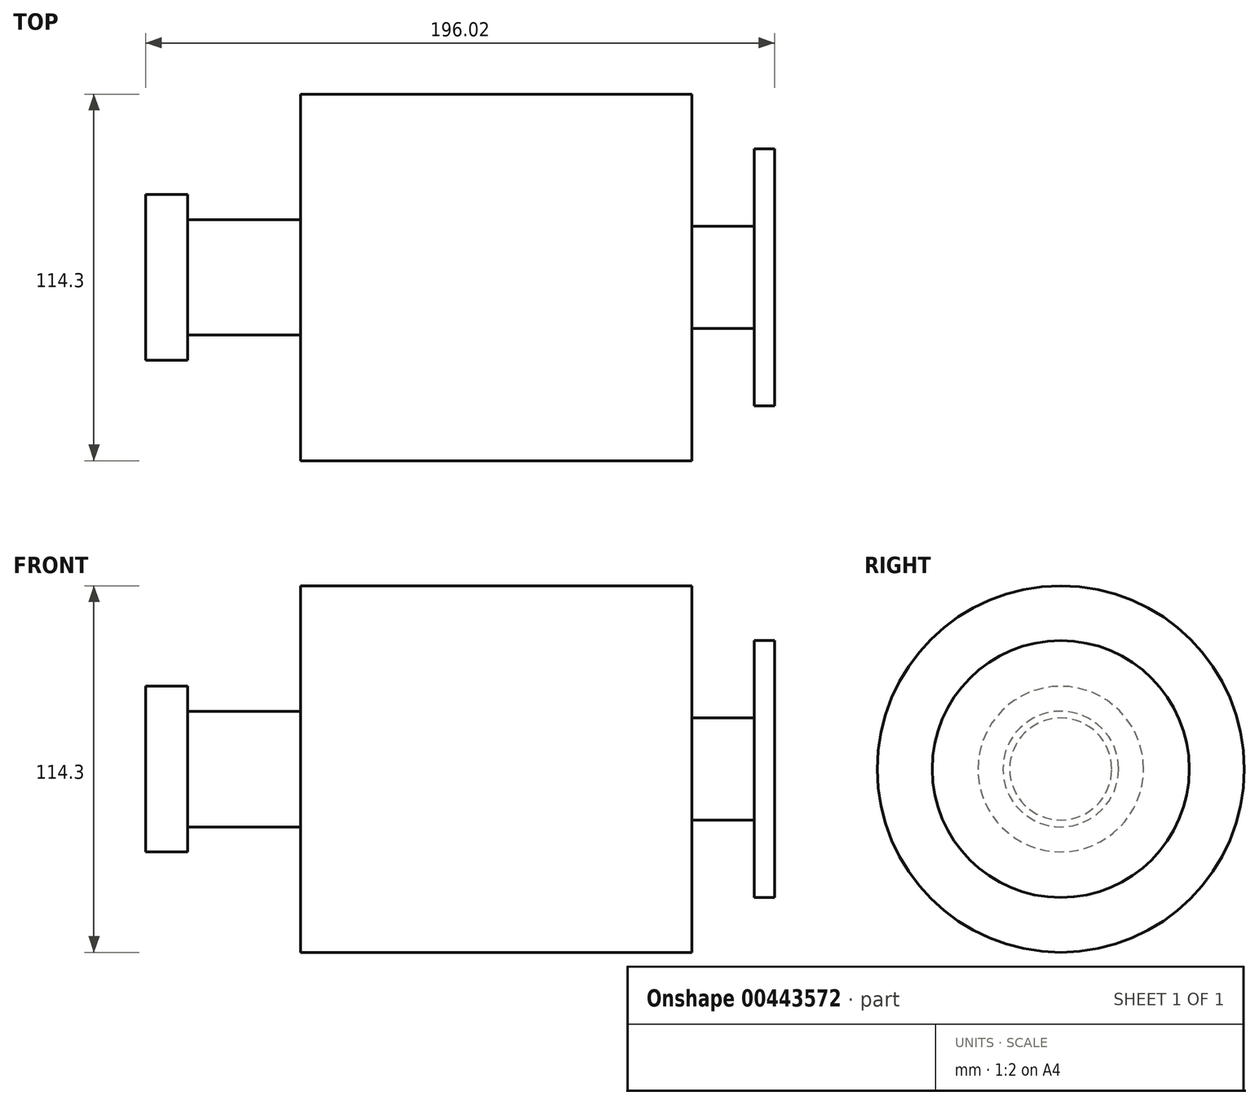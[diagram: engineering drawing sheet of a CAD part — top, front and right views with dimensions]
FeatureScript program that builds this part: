
annotation { "Feature Type Name" : "Feature", "Feature Type Description" : "" }
export const myFeature = defineFeature(function(context is Context, id is Id, definition is map)
    precondition{}
    {
        {
            var Q0;
            Q0=qCreatedBy(makeId("Front.planeOp"),FACE);
            var sketch = newSketch(context, id + "F0", { "sketchPlane" : qUnion([Q0])});
            skLineSegment(sketch, "E0", {"start": v(-60.96, 57.15) * mm, "end": v(60.96, 57.15) * mm});
            skLineSegment(sketch, "E1", {"start": v(-109.26, 25.8) * mm, "end": v(-96.16, 25.8) * mm});
            skLineSegment(sketch, "E2", {"start": v(-60.96, 57.15) * mm, "end": v(-60.96, 18.02) * mm});
            skLineSegment(sketch, "E3", {"start": v(-60.96, 18.02) * mm, "end": v(-96.16, 18.02) * mm});
            skLineSegment(sketch, "E4", {"start": v(-96.16, 18.02) * mm, "end": v(-96.16, 25.8) * mm});
            skLineSegment(sketch, "E5", {"start": v(-109.26, 25.8) * mm, "end": v(-109.26, 0) * mm});
            skLineSegment(sketch, "E6", {"start": v(80.46, 40.05) * mm, "end": v(86.76, 40.05) * mm});
            skLineSegment(sketch, "E7", {"start": v(60.96, 57.15) * mm, "end": v(60.96, 15.9) * mm});
            skLineSegment(sketch, "E8", {"start": v(60.96, 15.9) * mm, "end": v(80.46, 15.9) * mm});
            skLineSegment(sketch, "E9", {"start": v(80.46, 15.9) * mm, "end": v(80.46, 40.05) * mm});
            skLineSegment(sketch, "E10", {"start": v(86.76, 40.05) * mm, "end": v(86.76, 0) * mm});
            skLineSegment(sketch, "E11", {"start": v(86.76, 0) * mm, "end": v(-109.26, 0) * mm});
            skSolve(sketch);
        }
        {
            var Q0;
            Q0=makeQuery(id+"F0.imprint","IMPRINT",FACE,{"disambiguationData":[TD([[makeQuery(id+"F0.imprint","IMPRINT",EDGE,{"derivedFrom":sQuery(id+"F0.wireOp",EDGE,"E0")}),-1.0]])]});
            var Q1;
            Q1=sQuery(id+"F0.wireOp",EDGE,"E11");
            revolve(context, id + "F1", {"entities" : qUnion([Q0]), "axis" : qUnion([Q1]), "revolveType" : RevolveType.FULL});
        }
    });
